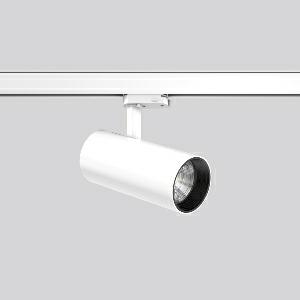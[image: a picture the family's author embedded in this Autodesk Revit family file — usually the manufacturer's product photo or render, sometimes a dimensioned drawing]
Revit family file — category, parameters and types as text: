
# Revit family: deecos_s_mini_742208_002_1_7f50
name_source: partatom
category: Lighting Fixtures
units: mm (PartAtom-declared; Revit-internal decimal feet)

## family parameters
Cut with Voids When Loaded = No
Host = Face
Light Source = No
Part Type = Normal
Room Calculation Point = No
Round Connector Dimension = Use Diameter
Shared = No

## types (1)
- DEECOS S mini (1 x LED Modul 940, 3000 lm, 4000)
    Apparent Load = 29 VA
    Approval mark = CE
    CIE Flux Codes = 98 100 100 100 100
    Color Rendering = 92
    Color Temperature = 4000
    Default Elevation = 1800 mm
    Description = Series: DEECOS S mini
LED surface-mounted projector in modern design with no visible cooling ribs. Housing: die-cast aluminium, powder-coated. Rotation range: 356°. Swivel range: 90°. Black plastic ring and recessed LED to prevent glare from the side. Optical assembly with lens made of plastic (polycarbonate) for the best homogeneous light distribution - can be changed without tools. Best colour rendering index Ra>90. With multi adaptor for 3-circuit tracks 230 V. Suitable for Track on ceiling, Wall track. High quality converter without flickering and stroboscopic effect. The following accessories can be mounted without use of tools: interchangeable lenses, decorative glasses, honeycomb louvre, clear and frosted diffusers, white interchangeable plastic ring. 
Colour: traffic white, matt (RAL 9016)
Diameter: 87 mm
Height: 214 mm
Lamp: LED
Socket: without socket
Colour temperature: 4000K
Colour rendering index (CRI): 92
System power: 29 W
Rated luminous flux: 3000 lm
Luminous efficiency: 103 lm/W
Control gear: Regulated power supply
Protection class: I
Type of protection: IP 20
    Height = 214 mm
    Lamp = 1 x LED Modul 940
    Lamp Light Flux = 3000 lm
    Lamp count = 1
    Length = 87 mm
    Lifetime = 50000 h
    Luminous efficacy = 103 lm/W
    Manufacturer = RZB
    ModVariant = No
    Model = 742208.002.1
    Mounting Place = Ceiling
    Mounting Type = Rail mounted
    Number of Poles = 1
    OnlyDefault = Yes
    Power Factor = 1
    Product Name = DEECOS S mini
    Product group = Track mounted projectors
    ProductGroupID = 301
    Protection Class = Protection class I
    Protection Degree = IP 20
    RLX_Detail_Level = 1
    RLX_Emergency_Light_Flux = 0 lm
    RLX_Emergency_Type = 0
    RLX_Emergency_Type_DB = No
    RlxData = <blob elided: 35673 chars, md5=464fc9fd>
    Socket = socket
    Standby Power = 0 W
    System Light Flux = 3000 lm
    System Power = 29 W
    Type Comments = Product without accessories
    Type Image = 741930.002.jpg
    URL = http://relux.com
    VarID = ---
    Voltage = 230 V
    Voltage Range = 220-240 V
    Weight = 0.00 kg
    Width = 0 mm  [stored 0 ft]

note: [stored X ft] marks values corroborated as IEEE doubles in the binary element streams (Revit-internal decimal feet)

## geometry (parser evidence)
native form markers: Blend x4, Sweep x12
no freeform markers — native parametric forms only
